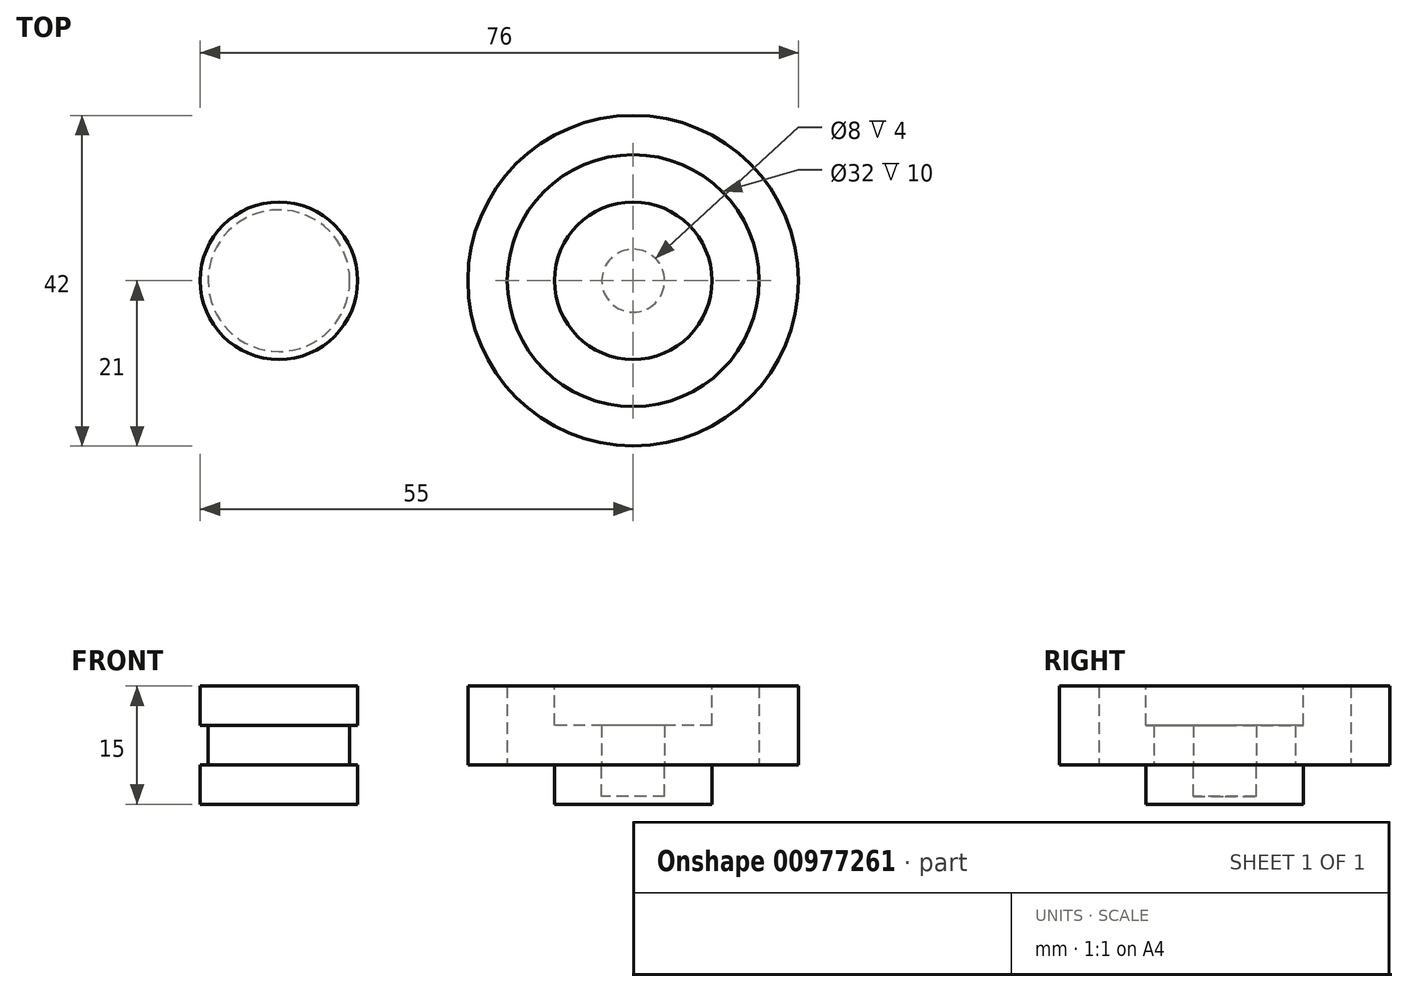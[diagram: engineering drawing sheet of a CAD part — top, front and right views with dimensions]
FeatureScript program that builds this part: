
annotation { "Feature Type Name" : "Feature", "Feature Type Description" : "" }
export const myFeature = defineFeature(function(context is Context, id is Id, definition is map)
    precondition{}
    {
        {
            var Q0;
            Q0=qCreatedBy(makeId("Top.planeOp"),FACE);
            var sketch = newSketch(context, id + "F0", { "sketchPlane" : qUnion([Q0])});
            skCircle(sketch, "E0", {"center": v(0, 0) * mm, "radius": 10 * mm});
            skCircle(sketch, "E1", {"center": v(0, 0) * mm, "radius": 4 * mm});
            skCircle(sketch, "E2", {"center": v(13, 0) * mm, "radius": 3 * mm});
            skCircle(sketch, "E3", {"center": v(0, 0) * mm, "radius": 16 * mm});
            skCircle(sketch, "E4", {"center": v(0, 0) * mm, "radius": 21 * mm});
            skCircle(sketch, "E5", {"center": v(-45, 0) * mm, "radius": 9 * mm});
            skCircle(sketch, "E6", {"center": v(-45, 0) * mm, "radius": 10 * mm});
            skSolve(sketch);
        }
        {
            var Q0;
            Q0=makeQuery(id+"F0.imprint","IMPRINT",FACE,{"disambiguationData":[TD([[makeQuery(id+"F0.imprint","IMPRINT",EDGE,{"derivedFrom":sQuery(id+"F0.wireOp",EDGE,"E0")}),1.0]])]});
            var Q1;
            Q1=makeQuery(id+"F0.imprint","IMPRINT",FACE,{"disambiguationData":[TD([[makeQuery(id+"F0.imprint","IMPRINT",EDGE,{"derivedFrom":sQuery(id+"F0.wireOp",EDGE,"E1")}),1.0]])]});
            extrude(context, id + "F1", {"entities" : qUnion([Q0, Q1]), "oppositeDirection" : true, "depth" : 5 * mm, "offsetDistance" : 25 * mm});
        }
        {
            var Q0;
            Q0=makeQuery(id+"F0.imprint","IMPRINT",FACE,{"disambiguationData":[TD([[makeQuery(id+"F0.imprint","IMPRINT",EDGE,{"derivedFrom":sQuery(id+"F0.wireOp",EDGE,"E1")}),1.0]])]});
            extrude(context, id + "F2", {"entities" : qUnion([Q0]), "depth" : 10 * mm, "offsetDistance" : 25 * mm});
        }
        {
            var Q0;
            Q0=makeQuery(id+"F2.opExtrude","CAP_FACE",FACE,{"disambiguationData":[OSD([sQuery(id+"F0.wireOp",EDGE,"E1")])],"isStart":false});
            var sketch = newSketch(context, id + "F3", { "sketchPlane" : qUnion([Q0])});
            skCircle(sketch, "E7", {"center": v(0, 0) * mm, "radius": 10 * mm});
            skSolve(sketch);
        }
        {
            var Q0;
            Q0=makeQuery(id+"F3.imprint","IMPRINT",FACE,{"disambiguationData":[TD([[makeQuery(id+"F3.imprint","IMPRINT",EDGE,{"derivedFrom":sQuery(id+"F3.wireOp",EDGE,"E7")}),1.0]])]});
            extrude(context, id + "F4", {"entities" : qUnion([Q0]), "operationType" : NewBodyOperationType.ADD, "oppositeDirection" : true, "depth" : 5 * mm, "offsetDistance" : 25 * mm});
        }
        {
            var Q0;
            Q0=makeQuery(id+"F0.imprint","IMPRINT",FACE,{"disambiguationData":[TD([[makeQuery(id+"F0.imprint","IMPRINT",EDGE,{"derivedFrom":sQuery(id+"F0.wireOp",EDGE,"E1")}),1.0]])]});
            extrude(context, id + "F5", {"entities" : qUnion([Q0]), "operationType" : NewBodyOperationType.REMOVE, "oppositeDirection" : true, "depth" : 4 * mm, "offsetDistance" : 25 * mm});
        }
        {
            var Q0;
            Q0=makeQuery(id+"F0.imprint","IMPRINT",FACE,{"disambiguationData":[TD([[makeQuery(id+"F0.imprint","IMPRINT",EDGE,{"derivedFrom":sQuery(id+"F0.wireOp",EDGE,"E3")}),-1.0]])]});
            extrude(context, id + "F6", {"entities" : qUnion([Q0]), "depth" : 10 * mm, "offsetDistance" : 25 * mm});
        }
        {
            var Q0;
            Q0=makeQuery(id+"F0.imprint","IMPRINT",FACE,{"disambiguationData":[TD([[makeQuery(id+"F0.imprint","IMPRINT",EDGE,{"derivedFrom":sQuery(id+"F0.wireOp",EDGE,"E5")}),-1.0]])]});
            var Q1;
            Q1=makeQuery(id+"F0.imprint","IMPRINT",FACE,{"disambiguationData":[TD([[makeQuery(id+"F0.imprint","IMPRINT",EDGE,{"derivedFrom":sQuery(id+"F0.wireOp",EDGE,"E5")}),1.0]])]});
            extrude(context, id + "F7", {"entities" : qUnion([Q0, Q1]), "oppositeDirection" : true, "depth" : 5 * mm, "offsetDistance" : 25 * mm});
        }
        {
            var Q0;
            Q0=makeQuery(id+"F0.imprint","IMPRINT",FACE,{"disambiguationData":[TD([[makeQuery(id+"F0.imprint","IMPRINT",EDGE,{"derivedFrom":sQuery(id+"F0.wireOp",EDGE,"E5")}),1.0]])]});
            cPlane(context, id + "F8", {"entities" : qUnion([Q0]), "cplaneType" : CPlaneType.OFFSET, "offset" : 5 * mm, "width" : 150 * mm, "height" : 150 * mm});
        }
        {
            var Q0;
            Q0=makeQuery(id+"F0.imprint","IMPRINT",FACE,{"disambiguationData":[TD([[makeQuery(id+"F0.imprint","IMPRINT",EDGE,{"derivedFrom":sQuery(id+"F0.wireOp",EDGE,"E5")}),1.0]])]});
            extrude(context, id + "F9", {"entities" : qUnion([Q0]), "operationType" : NewBodyOperationType.ADD, "depth" : 10 * mm, "offsetDistance" : 25 * mm});
        }
        {
            var Q0;
            Q0=qCreatedBy(id+"F8.planeOp",FACE);
            var sketch = newSketch(context, id + "F10", { "sketchPlane" : qUnion([Q0])});
            skPoint(sketch, "E8.0", {"position": v(-45, 0) * mm});
            skCircle(sketch, "E9", {"center": v(-45, 0) * mm, "radius": 10 * mm});
            skSolve(sketch);
        }
        {
            var Q0;
            Q0=makeQuery(id+"F10.imprint","IMPRINT",FACE,{"disambiguationData":[TD([[makeQuery(id+"F10.imprint","IMPRINT",EDGE,{"derivedFrom":sQuery(id+"F10.wireOp",EDGE,"E9")}),1.0]])]});
            extrude(context, id + "F11", {"entities" : qUnion([Q0]), "operationType" : NewBodyOperationType.ADD, "depth" : 5 * mm, "offsetDistance" : 25 * mm});
        }
    });
